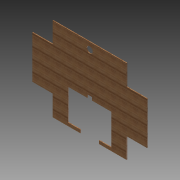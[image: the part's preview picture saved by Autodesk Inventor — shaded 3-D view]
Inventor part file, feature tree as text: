
AUTODESK INVENTOR PART (.ipt)
format: ipt  version: 2012 (Build 160160000, 160)  size: 120,832 bytes
history: native  units: in
note: dims shown in document units (in); Inventor stores cm internally (conversion verified against a paired STEP export)
features: extrude x1, sketch x1
ambient origin geometry x8: Origin, YZ Plane, XZ Plane, XY Plane, X Axis, Y Axis, Z Axis, Center Point
bodies: Solid1 (feature_tree)
feature tree (2):
  extrude  "Extrusion1"  Depth=27.0in
  sketch  "Sketch1"  dims[d0=37.0in d1=27.0in d2=23.75in d3=13.75in d4=6.625in d5=6.625in d6=6.625in d8=6.625in d9=0.25in d10=0.0in d11=6.0in d12=8.875in d13=8.875in d14=1.0in d15=14.0in d16=10.0in d17=1.0in d18=1.5in d19=2.0in d20=2.25in]
